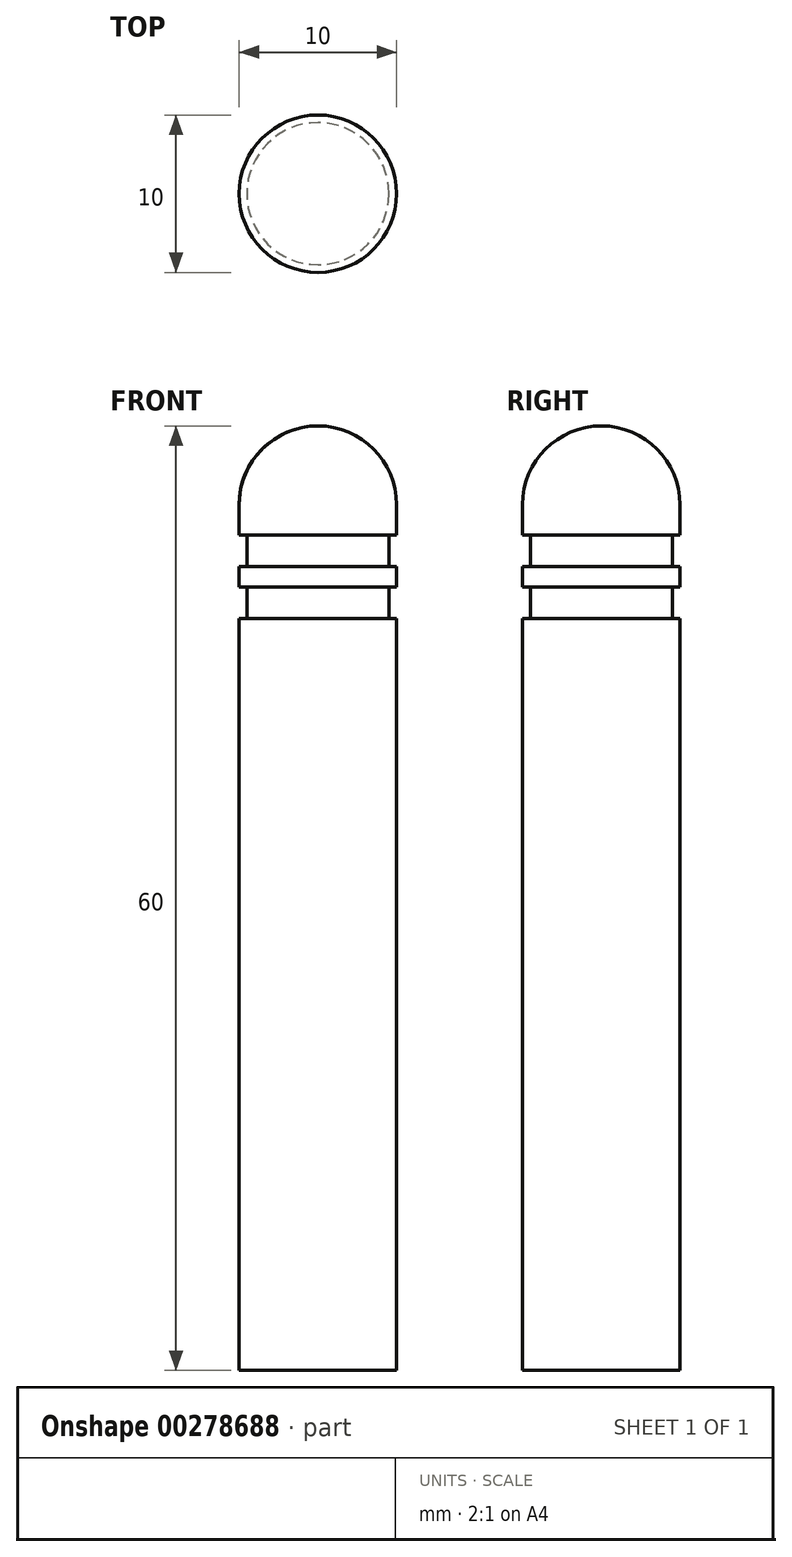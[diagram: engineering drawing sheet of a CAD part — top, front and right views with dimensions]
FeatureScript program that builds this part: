
annotation { "Feature Type Name" : "Feature", "Feature Type Description" : "" }
export const myFeature = defineFeature(function(context is Context, id is Id, definition is map)
    precondition{}
    {
        {
            var Q0;
            Q0=qCreatedBy(makeId("Front.planeOp"),FACE);
            var sketch = newSketch(context, id + "F0", { "sketchPlane" : qUnion([Q0])});
            skArc(sketch, "E0", {"start": v(0, 5) * mm, "mid": v(-3.54, 3.54) * mm, "end": v(-5, 0) * mm});
            skLineSegment(sketch, "E1", {"start": v(-5, -55) * mm, "end": v(0, -55) * mm});
            skLineSegment(sketch, "E2", {"start": v(0, -55) * mm, "end": v(0, 5) * mm});
            skLineSegment(sketch, "E3", {"start": v(-5, 0) * mm, "end": v(-5, -1.92) * mm});
            skLineSegment(sketch, "E4", {"start": v(-5, -1.92) * mm, "end": v(-4.51, -1.92) * mm});
            skLineSegment(sketch, "E5", {"start": v(-4.51, -1.92) * mm, "end": v(-4.51, -3.92) * mm});
            skLineSegment(sketch, "E6", {"start": v(-4.51, -3.92) * mm, "end": v(-5, -3.92) * mm});
            skLineSegment(sketch, "E7", {"start": v(-5, -3.92) * mm, "end": v(-5, -5.24) * mm});
            skLineSegment(sketch, "E8", {"start": v(-5, -5.24) * mm, "end": v(-4.51, -5.24) * mm});
            skLineSegment(sketch, "E9", {"start": v(-4.51, -5.24) * mm, "end": v(-4.51, -7.24) * mm});
            skLineSegment(sketch, "E10", {"start": v(-4.51, -7.24) * mm, "end": v(-5, -7.24) * mm});
            skLineSegment(sketch, "E11", {"start": v(-5, -7.24) * mm, "end": v(-5, -55) * mm});
            skSolve(sketch);
        }
        {
            var Q0;
            Q0=makeQuery(id+"F0.imprint","IMPRINT",FACE,{"disambiguationData":[TD([[makeQuery(id+"F0.imprint","IMPRINT",EDGE,{"derivedFrom":sQuery(id+"F0.wireOp",EDGE,"E0")}),1.0]])]});
            var Q1;
            Q1=sQuery(id+"F0.wireOp",EDGE,"E2");
            revolve(context, id + "F1", {"entities" : qUnion([Q0]), "axis" : qUnion([Q1]), "revolveType" : RevolveType.FULL});
        }
    });
